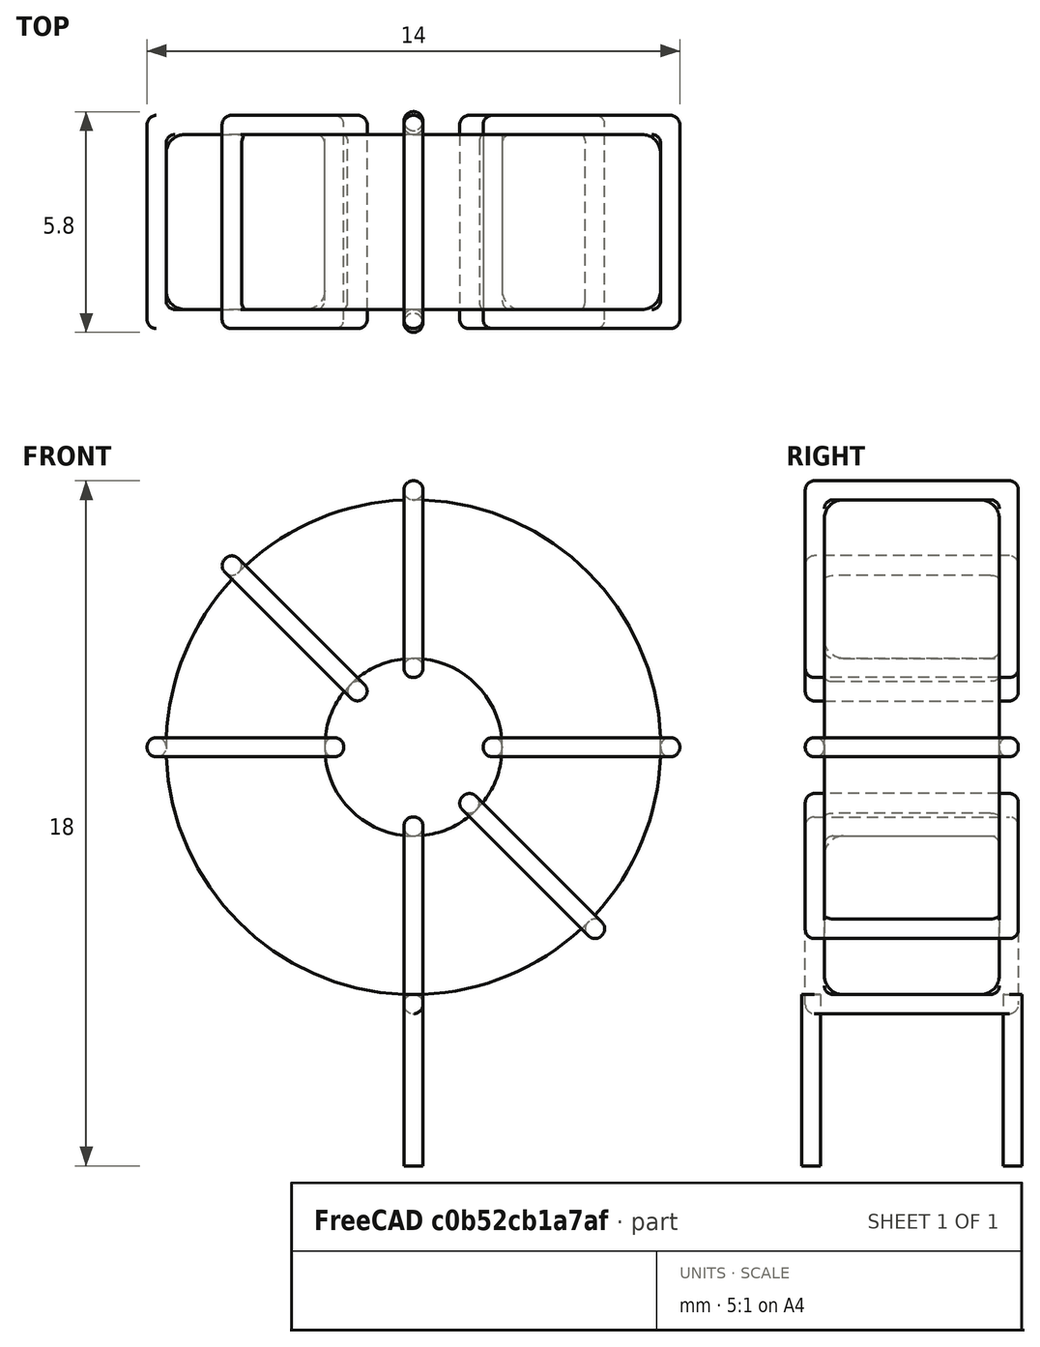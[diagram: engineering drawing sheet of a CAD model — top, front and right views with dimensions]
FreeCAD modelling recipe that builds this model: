
FCSTD DOCUMENT  (FreeCAD 0.16R6703 (Git))
Label: L_Toroid_Vertical_L14.0mm_W5.6mm_P5.30mm_Bourns_5700series
License: All rights reserved
LicenseURL: http://en.wikipedia.org/wiki/All_rights_reserved
objects: Sketcher::SketchObject×6, PartDesign::Pad×6, PartDesign::Fillet×5, Spreadsheet::Sheet×1
note: 23 computed .brp shape members not serialized (recipe doc carries the construction recipe); baked Part::Feature solids carry a one-line shape summary decoded from their .brp

FEATURE [Spreadsheet::Sheet] Spreadsheet  label="dimensions"
  cells = A1=Wx; B1(Wx)=14; C1(WW)=4.666666666666667; D1=14; A2=Wy; B2(Wy)=5.6; D2=5.6; A3=RM; B3(RMx)=5.3; C3(RMy)=0; A4=d_wire; B4(d_wire)=0.5; A5=H; B5(H)=14; A6=offsetx; B6(offsetx)=7
FEATURE [Sketcher::SketchObject] Sketch
  Placement = pos=(0,-2.65,0) rot=(1,0,0;1.5708rad)
  expr: Placement.Base.y = -Spreadsheet.RMx / 2
  expr: Constraints[0] = Spreadsheet.Wx / 2 - Spreadsheet.d_wire
  expr: Constraints[4] = Spreadsheet.WW / 2
  expr: Constraints[2] = Spreadsheet.Wx / 2 + Spreadsheet.d_wire + 0.5
  sketch-geometry (2):
    g0: Circle CenterX=0 CenterY=8 CenterZ=0 NormalX=0 NormalY=0 NormalZ=1 Radius=6.5
    g1: Circle CenterX=0 CenterY=8 CenterZ=0 NormalX=0 NormalY=0 NormalZ=1 Radius=2.33333
  constraints (5):
    c: Radius(g0) = 6.5
    c: DistanceX(g-1,g0) = 0
    c: DistanceY(g-1,g0) = 8
    c: Coincident(g1,g0)
    c: Radius(g1) = 2.33333
FEATURE [PartDesign::Pad] Pad
  Length = 4.6
  Length2 = 100
  Midplane = true
  Placement = pos=(0,-2.65,0) rot=(1,0,0;1.5708rad)
  Sketch = -> Sketch
  Type = 0
  expr: Length = Spreadsheet.Wy - 2 * Spreadsheet.d_wire
FEATURE [Sketcher::SketchObject] Sketch001
  Placement = pos=(0,0,1) rot=(0,0,1;0rad)
  expr: Placement.Base.z = 0.5 + Spreadsheet.d_wire
  expr: Constraints[4] = Spreadsheet.RMy
  expr: Constraints[2] = -Spreadsheet.RMx
  expr: Constraints[1] = Spreadsheet.d_wire / 2
  sketch-geometry (2):
    g0: Circle CenterX=0 CenterY=0 CenterZ=0 NormalX=0 NormalY=0 NormalZ=1 Radius=0.25
    g1: Circle CenterX=0 CenterY=-5.3 CenterZ=0 NormalX=0 NormalY=0 NormalZ=1 Radius=0.25
  constraints (5):
    c: Equal(g0,g1)
    c: Radius(g0) = 0.25
    c: DistanceY(g-1,g1) = -5.3
    c: Coincident(g0,g-1)
    c: DistanceX(g-1,g1) = 0
FEATURE [PartDesign::Pad] Pad001
  Length = 0.5
  Length2 = 4
  Placement = pos=(0,0,1) rot=(0,0,1;0rad)
  Reversed = true
  Sketch = -> Sketch001
  Type = 4
  expr: Length2 = 3.5 + Spreadsheet.d_wire
  expr: Length = Spreadsheet.d_wire
FEATURE [PartDesign::Fillet] Fillet
  Base = -> Pad [Edge6,Edge3,Edge2]
  Placement = pos=(0,-2.65,0) rot=(1,0,0;1.5708rad)
  Radius = 0.5
FEATURE [Sketcher::SketchObject] Sketch003
  Placement = pos=(0,0.15,8) rot=(1,0,0;3.14159rad)
  expr: Constraints[18] = Spreadsheet.d_wire
  expr: Constraints[16] = Spreadsheet.d_wire
  expr: Constraints[19] = Spreadsheet.d_wire
  expr: Constraints[17] = Spreadsheet.d_wire
  expr: Placement.Base.y = -1 * (Spreadsheet.RMx - Spreadsheet.Wy) / 2
  expr: Constraints[21] = (Spreadsheet.Wx - Spreadsheet.WW) / 2 - Spreadsheet.d_wire
  expr: Constraints[22] = Spreadsheet.Wx / 2 - Spreadsheet.d_wire
  expr: Constraints[43] = Spreadsheet.d_wire
  expr: Constraints[48] = Spreadsheet.Wx - Spreadsheet.d_wire * 2
  expr: Constraints[49] = Spreadsheet.Wy
  expr: Placement.Base.z = Spreadsheet.Wx / 2 + Spreadsheet.d_wire + 0.5
  sketch-geometry (16):
    g0: LineSegment StartX=-1.83333 StartY=0 StartZ=0 EndX=-7 EndY=0 EndZ=0
    g1: LineSegment StartX=-7 StartY=0 StartZ=0 EndX=-7 EndY=5.6 EndZ=0
    g2: LineSegment StartX=-7 StartY=5.6 StartZ=0 EndX=-1.83333 EndY=5.6 EndZ=0
    g3: LineSegment StartX=-1.83333 StartY=5.6 StartZ=0 EndX=-1.83333 EndY=0 EndZ=0
    g4: LineSegment StartX=-6.5 StartY=5.1 StartZ=0 EndX=-2.33333 EndY=5.1 EndZ=0
    g5: LineSegment StartX=-2.33333 StartY=5.1 StartZ=0 EndX=-2.33333 EndY=0.5 EndZ=0
    g6: LineSegment StartX=-2.33333 StartY=0.5 StartZ=0 EndX=-6.5 EndY=0.5 EndZ=0
    g7: LineSegment StartX=-6.5 StartY=0.5 StartZ=0 EndX=-6.5 EndY=5.1 EndZ=0
    g8: LineSegment StartX=1.83333 StartY=5.6 StartZ=0 EndX=7 EndY=5.6 EndZ=0
    g9: LineSegment StartX=7 StartY=5.6 StartZ=0 EndX=7 EndY=0 EndZ=0
    g10: LineSegment StartX=7 StartY=0 StartZ=0 EndX=1.83333 EndY=0 EndZ=0
    g11: LineSegment StartX=1.83333 StartY=0 StartZ=0 EndX=1.83333 EndY=5.6 EndZ=0
    g12: LineSegment StartX=2.33333 StartY=5.1 StartZ=0 EndX=6.5 EndY=5.1 EndZ=0
    g13: LineSegment StartX=6.5 StartY=5.1 StartZ=0 EndX=6.5 EndY=0.5 EndZ=0
    g14: LineSegment StartX=6.5 StartY=0.5 StartZ=0 EndX=2.33333 EndY=0.5 EndZ=0
    g15: LineSegment StartX=2.33333 StartY=0.5 StartZ=0 EndX=2.33333 EndY=5.1 EndZ=0
  constraints (50):
    c: Horizontal(g0)
    c: Coincident(g1,g0)
    c: Vertical(g1)
    c: Coincident(g2,g1)
    c: Horizontal(g2)
    c: Coincident(g3,g2)
    c: Coincident(g3,g0)
    c: Vertical(g3)
    c: Coincident(g4,g5)
    c: Coincident(g5,g6)
    c: Coincident(g6,g7)
    c: Coincident(g7,g4)
    c: Horizontal(g4)
    c: Horizontal(g6)
    c: Vertical(g5)
    c: Vertical(g7)
    c: DistanceX(g1,g4) = 0.5
    c: DistanceY(g4,g1) = 0.5
    c: DistanceX(g5,g0) = 0.5
    c: DistanceY(g0,g5) = 0.5
    c: DistanceY(g-1,g0) = 0
    c: DistanceX(g6,g6) = 4.16667
    c: DistanceX(g6,g-1) = 6.5
    c: Coincident(g8,g9)
    c: Coincident(g9,g10)
    c: Coincident(g10,g11)
    c: Coincident(g11,g8)
    c: Horizontal(g8)
    c: Horizontal(g10)
    c: Vertical(g9)
    c: Vertical(g11)
    c: Coincident(g12,g13)
    c: Coincident(g13,g14)
    c: Coincident(g14,g15)
    c: Coincident(g15,g12)
    c: Horizontal(g12)
    c: Horizontal(g14)
    c: Vertical(g13)
    c: Vertical(g15)
    c: DistanceY(g8,g2) = 0
    c: DistanceY(g10,g0) = 0
    c: DistanceY(g14,g5) = 0
    c: DistanceY(g12,g4) = 0
    c: DistanceX(g8,g12) = 0.5
    c: Equal(g8,g2)
    c: Equal(g12,g4)
    c: Equal(g9,g1)
    c: Equal(g13,g7)
    c: DistanceX(g4,g12) = 13
    c: DistanceY(g0,g1) = 5.6
FEATURE [PartDesign::Pad] Pad002
  Length = 0.5
  Length2 = 100
  Midplane = true
  Placement = pos=(0,0.15,8) rot=(1,0,0;3.14159rad)
  Sketch = -> Sketch003
  Type = 0
  expr: Length = Spreadsheet.d_wire
FEATURE [PartDesign::Fillet] Fillet001
  Base = -> Pad002 [Edge38,Edge41,Edge42,Edge43,Edge29,Edge32,Edge33,Edge34,Edge25,Edge35,Edge36,Edge13,Edge14,Edge15,Edge16,Edge17,Edge18,Edge19,Edge1,Edge2,Edge3,Edge4,Edge5,Edge6,Edge7,Edge37,Edge39,Edge40,Edge20,Edge23,Edge24,Edge21,Edge22,Edge8,Edge9,Edge10,Edge11,Edge12,Edge26,Edge27,+8 more]
  Placement = pos=(0,0.15,8) rot=(1,0,0;3.14159rad)
  Radius = 0.235
  expr: Radius = Spreadsheet.d_wire * 0.47
FEATURE [Sketcher::SketchObject] Sketch004
  Placement = pos=(0,0.15,8) rot=(0.92388,0,0.382683;3.14159rad)
  expr: Constraints[18] = Spreadsheet.d_wire
  expr: Constraints[16] = Spreadsheet.d_wire
  expr: Constraints[19] = Spreadsheet.d_wire
  expr: Constraints[17] = Spreadsheet.d_wire
  expr: Placement.Base.y = -1 * (Spreadsheet.RMx - Spreadsheet.Wy) / 2
  expr: Constraints[21] = (Spreadsheet.Wx - Spreadsheet.WW) / 2 - Spreadsheet.d_wire
  expr: Constraints[22] = Spreadsheet.Wx / 2 - Spreadsheet.d_wire
  expr: Constraints[43] = Spreadsheet.d_wire
  expr: Constraints[48] = Spreadsheet.Wx - 2 * Spreadsheet.d_wire
  expr: Constraints[49] = Spreadsheet.Wy
  expr: Placement.Base.z = Spreadsheet.Wx / 2 + Spreadsheet.d_wire + 0.5
  sketch-geometry (16):
    g0: LineSegment StartX=-1.83333 StartY=0 StartZ=0 EndX=-7 EndY=0 EndZ=0
    g1: LineSegment StartX=-7 StartY=0 StartZ=0 EndX=-7 EndY=5.6 EndZ=0
    g2: LineSegment StartX=-7 StartY=5.6 StartZ=0 EndX=-1.83333 EndY=5.6 EndZ=0
    g3: LineSegment StartX=-1.83333 StartY=5.6 StartZ=0 EndX=-1.83333 EndY=0 EndZ=0
    g4: LineSegment StartX=-6.5 StartY=5.1 StartZ=0 EndX=-2.33333 EndY=5.1 EndZ=0
    g5: LineSegment StartX=-2.33333 StartY=5.1 StartZ=0 EndX=-2.33333 EndY=0.5 EndZ=0
    g6: LineSegment StartX=-2.33333 StartY=0.5 StartZ=0 EndX=-6.5 EndY=0.5 EndZ=0
    g7: LineSegment StartX=-6.5 StartY=0.5 StartZ=0 EndX=-6.5 EndY=5.1 EndZ=0
    g8: LineSegment StartX=1.83333 StartY=5.6 StartZ=0 EndX=7 EndY=5.6 EndZ=0
    g9: LineSegment StartX=7 StartY=5.6 StartZ=0 EndX=7 EndY=0 EndZ=0
    g10: LineSegment StartX=7 StartY=0 StartZ=0 EndX=1.83333 EndY=0 EndZ=0
    g11: LineSegment StartX=1.83333 StartY=0 StartZ=0 EndX=1.83333 EndY=5.6 EndZ=0
    g12: LineSegment StartX=2.33333 StartY=5.1 StartZ=0 EndX=6.5 EndY=5.1 EndZ=0
    g13: LineSegment StartX=6.5 StartY=5.1 StartZ=0 EndX=6.5 EndY=0.5 EndZ=0
    g14: LineSegment StartX=6.5 StartY=0.5 StartZ=0 EndX=2.33333 EndY=0.5 EndZ=0
    g15: LineSegment StartX=2.33333 StartY=0.5 StartZ=0 EndX=2.33333 EndY=5.1 EndZ=0
  constraints (50):
    c: Horizontal(g0)
    c: Coincident(g1,g0)
    c: Vertical(g1)
    c: Coincident(g2,g1)
    c: Horizontal(g2)
    c: Coincident(g3,g2)
    c: Coincident(g3,g0)
    c: Vertical(g3)
    c: Coincident(g4,g5)
    c: Coincident(g5,g6)
    c: Coincident(g6,g7)
    c: Coincident(g7,g4)
    c: Horizontal(g4)
    c: Horizontal(g6)
    c: Vertical(g5)
    c: Vertical(g7)
    c: DistanceX(g1,g4) = 0.5
    c: DistanceY(g4,g1) = 0.5
    c: DistanceX(g5,g0) = 0.5
    c: DistanceY(g0,g5) = 0.5
    c: DistanceY(g-1,g0) = 0
    c: DistanceX(g6,g6) = 4.16667
    c: DistanceX(g6,g-1) = 6.5
    c: Coincident(g8,g9)
    c: Coincident(g9,g10)
    c: Coincident(g10,g11)
    c: Coincident(g11,g8)
    c: Horizontal(g8)
    c: Horizontal(g10)
    c: Vertical(g9)
    c: Vertical(g11)
    c: Coincident(g12,g13)
    c: Coincident(g13,g14)
    c: Coincident(g14,g15)
    c: Coincident(g15,g12)
    c: Horizontal(g12)
    c: Horizontal(g14)
    c: Vertical(g13)
    c: Vertical(g15)
    c: DistanceY(g8,g2) = 0
    c: DistanceY(g10,g0) = 0
    c: DistanceY(g14,g5) = 0
    c: DistanceY(g12,g4) = 0
    c: DistanceX(g8,g12) = 0.5
    c: Equal(g8,g2)
    c: Equal(g12,g4)
    c: Equal(g9,g1)
    c: Equal(g13,g7)
    c: DistanceX(g4,g12) = 13
    c: DistanceY(g0,g1) = 5.6
FEATURE [PartDesign::Pad] Pad003
  Length = 0.5
  Length2 = 100
  Midplane = true
  Placement = pos=(0,0.15,8) rot=(0.92388,0,0.382683;3.14159rad)
  Sketch = -> Sketch004
  Type = 0
  expr: Length = Spreadsheet.d_wire
FEATURE [PartDesign::Fillet] Fillet002
  Base = -> Pad003 [Edge38,Edge41,Edge42,Edge43,Edge29,Edge32,Edge33,Edge34,Edge25,Edge35,Edge36,Edge13,Edge14,Edge15,Edge16,Edge17,Edge18,Edge19,Edge1,Edge2,Edge3,Edge4,Edge5,Edge6,Edge7,Edge37,Edge39,Edge40,Edge20,Edge23,Edge24,Edge21,Edge22,Edge8,Edge9,Edge10,Edge11,Edge12,Edge26,Edge27,+8 more]
  Placement = pos=(0,0.15,8) rot=(0.92388,0,0.382683;3.14159rad)
  Radius = 0.235
  expr: Radius = Spreadsheet.d_wire * 0.47
FEATURE [Sketcher::SketchObject] Sketch005
  Placement = pos=(0,0.15,8) rot=(0.92388,0,-0.382683;3.14159rad)
  expr: Constraints[18] = Spreadsheet.d_wire
  expr: Constraints[16] = Spreadsheet.d_wire
  expr: Constraints[19] = Spreadsheet.d_wire
  expr: Constraints[17] = Spreadsheet.d_wire
  expr: Placement.Base.y = -1 * (Spreadsheet.RMx - Spreadsheet.Wy) / 2
  expr: Constraints[21] = (Spreadsheet.Wx - Spreadsheet.WW) / 2 - Spreadsheet.d_wire
  expr: Constraints[22] = Spreadsheet.Wx / 2 - Spreadsheet.d_wire
  expr: Constraints[43] = Spreadsheet.d_wire
  expr: Constraints[48] = Spreadsheet.Wx - 2 * Spreadsheet.d_wire
  expr: Constraints[49] = Spreadsheet.Wy
  expr: Placement.Base.z = Spreadsheet.Wx / 2 + Spreadsheet.d_wire + 0.5
  sketch-geometry (16):
    g0: LineSegment StartX=-1.83333 StartY=0 StartZ=0 EndX=-7 EndY=0 EndZ=0
    g1: LineSegment StartX=-7 StartY=0 StartZ=0 EndX=-7 EndY=5.6 EndZ=0
    g2: LineSegment StartX=-7 StartY=5.6 StartZ=0 EndX=-1.83333 EndY=5.6 EndZ=0
    g3: LineSegment StartX=-1.83333 StartY=5.6 StartZ=0 EndX=-1.83333 EndY=0 EndZ=0
    g4: LineSegment StartX=-6.5 StartY=5.1 StartZ=0 EndX=-2.33333 EndY=5.1 EndZ=0
    g5: LineSegment StartX=-2.33333 StartY=5.1 StartZ=0 EndX=-2.33333 EndY=0.5 EndZ=0
    g6: LineSegment StartX=-2.33333 StartY=0.5 StartZ=0 EndX=-6.5 EndY=0.5 EndZ=0
    g7: LineSegment StartX=-6.5 StartY=0.5 StartZ=0 EndX=-6.5 EndY=5.1 EndZ=0
    g8: LineSegment StartX=1.83333 StartY=5.6 StartZ=0 EndX=7 EndY=5.6 EndZ=0
    g9: LineSegment StartX=7 StartY=5.6 StartZ=0 EndX=7 EndY=0 EndZ=0
    g10: LineSegment StartX=7 StartY=0 StartZ=0 EndX=1.83333 EndY=0 EndZ=0
    g11: LineSegment StartX=1.83333 StartY=0 StartZ=0 EndX=1.83333 EndY=5.6 EndZ=0
    g12: LineSegment StartX=2.33333 StartY=5.1 StartZ=0 EndX=6.5 EndY=5.1 EndZ=0
    g13: LineSegment StartX=6.5 StartY=5.1 StartZ=0 EndX=6.5 EndY=0.5 EndZ=0
    g14: LineSegment StartX=6.5 StartY=0.5 StartZ=0 EndX=2.33333 EndY=0.5 EndZ=0
    g15: LineSegment StartX=2.33333 StartY=0.5 StartZ=0 EndX=2.33333 EndY=5.1 EndZ=0
  constraints (50):
    c: Horizontal(g0)
    c: Coincident(g1,g0)
    c: Vertical(g1)
    c: Coincident(g2,g1)
    c: Horizontal(g2)
    c: Coincident(g3,g2)
    c: Coincident(g3,g0)
    c: Vertical(g3)
    c: Coincident(g4,g5)
    c: Coincident(g5,g6)
    c: Coincident(g6,g7)
    c: Coincident(g7,g4)
    c: Horizontal(g4)
    c: Horizontal(g6)
    c: Vertical(g5)
    c: Vertical(g7)
    c: DistanceX(g1,g4) = 0.5
    c: DistanceY(g4,g1) = 0.5
    c: DistanceX(g5,g0) = 0.5
    c: DistanceY(g0,g5) = 0.5
    c: DistanceY(g-1,g0) = 0
    c: DistanceX(g6,g6) = 4.16667
    c: DistanceX(g6,g-1) = 6.5
    c: Coincident(g8,g9)
    c: Coincident(g9,g10)
    c: Coincident(g10,g11)
    c: Coincident(g11,g8)
    c: Horizontal(g8)
    c: Horizontal(g10)
    c: Vertical(g9)
    c: Vertical(g11)
    c: Coincident(g12,g13)
    c: Coincident(g13,g14)
    c: Coincident(g14,g15)
    c: Coincident(g15,g12)
    c: Horizontal(g12)
    c: Horizontal(g14)
    c: Vertical(g13)
    c: Vertical(g15)
    c: DistanceY(g8,g2) = 0
    c: DistanceY(g10,g0) = 0
    c: DistanceY(g14,g5) = 0
    c: DistanceY(g12,g4) = 0
    c: DistanceX(g8,g12) = 0.5
    c: Equal(g8,g2)
    c: Equal(g12,g4)
    c: Equal(g9,g1)
    c: Equal(g13,g7)
    c: DistanceX(g4,g12) = 13
    c: DistanceY(g0,g1) = 5.6
FEATURE [PartDesign::Pad] Pad004
  Length = 0.5
  Length2 = 100
  Midplane = true
  Placement = pos=(0,0.15,8) rot=(0.92388,0,-0.382683;3.14159rad)
  Sketch = -> Sketch005
  Type = 0
  expr: Length = Spreadsheet.d_wire
FEATURE [PartDesign::Fillet] Fillet003
  Base = -> Pad004 [Edge38,Edge41,Edge42,Edge43,Edge29,Edge32,Edge33,Edge34,Edge25,Edge35,Edge36,Edge13,Edge14,Edge15,Edge16,Edge17,Edge18,Edge19,Edge1,Edge2,Edge3,Edge4,Edge5,Edge6,Edge7,Edge37,Edge39,Edge40,Edge20,Edge23,Edge24,Edge21,Edge22,Edge8,Edge9,Edge10,Edge11,Edge12,Edge26,Edge27,+8 more]
  Placement = pos=(0,0.15,8) rot=(0.92388,0,-0.382683;3.14159rad)
  Radius = 0.235
  expr: Radius = Spreadsheet.d_wire * 0.47
FEATURE [Sketcher::SketchObject] Sketch006
  Placement = pos=(0,0.15,8) rot=(0.707107,0,0.707107;3.14159rad)
  expr: Constraints[18] = Spreadsheet.d_wire
  expr: Constraints[16] = Spreadsheet.d_wire
  expr: Constraints[19] = Spreadsheet.d_wire
  expr: Constraints[17] = Spreadsheet.d_wire
  expr: Placement.Base.y = -1 * (Spreadsheet.RMx - Spreadsheet.Wy) / 2
  expr: Constraints[21] = (Spreadsheet.Wx - Spreadsheet.WW) / 2 - Spreadsheet.d_wire
  expr: Constraints[22] = Spreadsheet.Wx / 2 - Spreadsheet.d_wire
  expr: Constraints[43] = Spreadsheet.d_wire
  expr: Constraints[48] = Spreadsheet.Wx - Spreadsheet.d_wire * 2
  expr: Constraints[49] = Spreadsheet.Wy
  expr: Placement.Base.z = Spreadsheet.Wx / 2 + Spreadsheet.d_wire + 0.5
  sketch-geometry (16):
    g0: LineSegment StartX=-1.83333 StartY=0 StartZ=0 EndX=-7 EndY=0 EndZ=0
    g1: LineSegment StartX=-7 StartY=0 StartZ=0 EndX=-7 EndY=5.6 EndZ=0
    g2: LineSegment StartX=-7 StartY=5.6 StartZ=0 EndX=-1.83333 EndY=5.6 EndZ=0
    g3: LineSegment StartX=-1.83333 StartY=5.6 StartZ=0 EndX=-1.83333 EndY=0 EndZ=0
    g4: LineSegment StartX=-6.5 StartY=5.1 StartZ=0 EndX=-2.33333 EndY=5.1 EndZ=0
    g5: LineSegment StartX=-2.33333 StartY=5.1 StartZ=0 EndX=-2.33333 EndY=0.5 EndZ=0
    g6: LineSegment StartX=-2.33333 StartY=0.5 StartZ=0 EndX=-6.5 EndY=0.5 EndZ=0
    g7: LineSegment StartX=-6.5 StartY=0.5 StartZ=0 EndX=-6.5 EndY=5.1 EndZ=0
    g8: LineSegment StartX=1.83333 StartY=5.6 StartZ=0 EndX=7 EndY=5.6 EndZ=0
    g9: LineSegment StartX=7 StartY=5.6 StartZ=0 EndX=7 EndY=0 EndZ=0
    g10: LineSegment StartX=7 StartY=0 StartZ=0 EndX=1.83333 EndY=0 EndZ=0
    g11: LineSegment StartX=1.83333 StartY=0 StartZ=0 EndX=1.83333 EndY=5.6 EndZ=0
    g12: LineSegment StartX=2.33333 StartY=5.1 StartZ=0 EndX=6.5 EndY=5.1 EndZ=0
    g13: LineSegment StartX=6.5 StartY=5.1 StartZ=0 EndX=6.5 EndY=0.5 EndZ=0
    g14: LineSegment StartX=6.5 StartY=0.5 StartZ=0 EndX=2.33333 EndY=0.5 EndZ=0
    g15: LineSegment StartX=2.33333 StartY=0.5 StartZ=0 EndX=2.33333 EndY=5.1 EndZ=0
  constraints (50):
    c: Horizontal(g0)
    c: Coincident(g1,g0)
    c: Vertical(g1)
    c: Coincident(g2,g1)
    c: Horizontal(g2)
    c: Coincident(g3,g2)
    c: Coincident(g3,g0)
    c: Vertical(g3)
    c: Coincident(g4,g5)
    c: Coincident(g5,g6)
    c: Coincident(g6,g7)
    c: Coincident(g7,g4)
    c: Horizontal(g4)
    c: Horizontal(g6)
    c: Vertical(g5)
    c: Vertical(g7)
    c: DistanceX(g1,g4) = 0.5
    c: DistanceY(g4,g1) = 0.5
    c: DistanceX(g5,g0) = 0.5
    c: DistanceY(g0,g5) = 0.5
    c: DistanceY(g-1,g0) = 0
    c: DistanceX(g6,g6) = 4.16667
    c: DistanceX(g6,g-1) = 6.5
    c: Coincident(g8,g9)
    c: Coincident(g9,g10)
    c: Coincident(g10,g11)
    c: Coincident(g11,g8)
    c: Horizontal(g8)
    c: Horizontal(g10)
    c: Vertical(g9)
    c: Vertical(g11)
    c: Coincident(g12,g13)
    c: Coincident(g13,g14)
    c: Coincident(g14,g15)
    c: Coincident(g15,g12)
    c: Horizontal(g12)
    c: Horizontal(g14)
    c: Vertical(g13)
    c: Vertical(g15)
    c: DistanceY(g8,g2) = 0
    c: DistanceY(g10,g0) = 0
    c: DistanceY(g14,g5) = 0
    c: DistanceY(g12,g4) = 0
    c: DistanceX(g8,g12) = 0.5
    c: Equal(g8,g2)
    c: Equal(g12,g4)
    c: Equal(g9,g1)
    c: Equal(g13,g7)
    c: DistanceX(g4,g12) = 13
    c: DistanceY(g0,g1) = 5.6
FEATURE [PartDesign::Pad] Pad005
  Length = 0.5
  Length2 = 100
  Midplane = true
  Placement = pos=(0,0.15,8) rot=(0.707107,0,0.707107;3.14159rad)
  Sketch = -> Sketch006
  Type = 0
  expr: Length = Spreadsheet.d_wire
FEATURE [PartDesign::Fillet] Fillet004
  Base = -> Pad005 [Edge38,Edge41,Edge42,Edge43,Edge29,Edge32,Edge33,Edge34,Edge25,Edge35,Edge36,Edge13,Edge14,Edge15,Edge16,Edge17,Edge18,Edge19,Edge1,Edge2,Edge3,Edge4,Edge5,Edge6,Edge7,Edge37,Edge39,Edge40,Edge20,Edge23,Edge24,Edge21,Edge22,Edge8,Edge9,Edge10,Edge11,Edge12,Edge26,Edge27,+8 more]
  Placement = pos=(0,0.15,8) rot=(0.707107,0,0.707107;3.14159rad)
  Radius = 0.235
  expr: Radius = Spreadsheet.d_wire * 0.47
